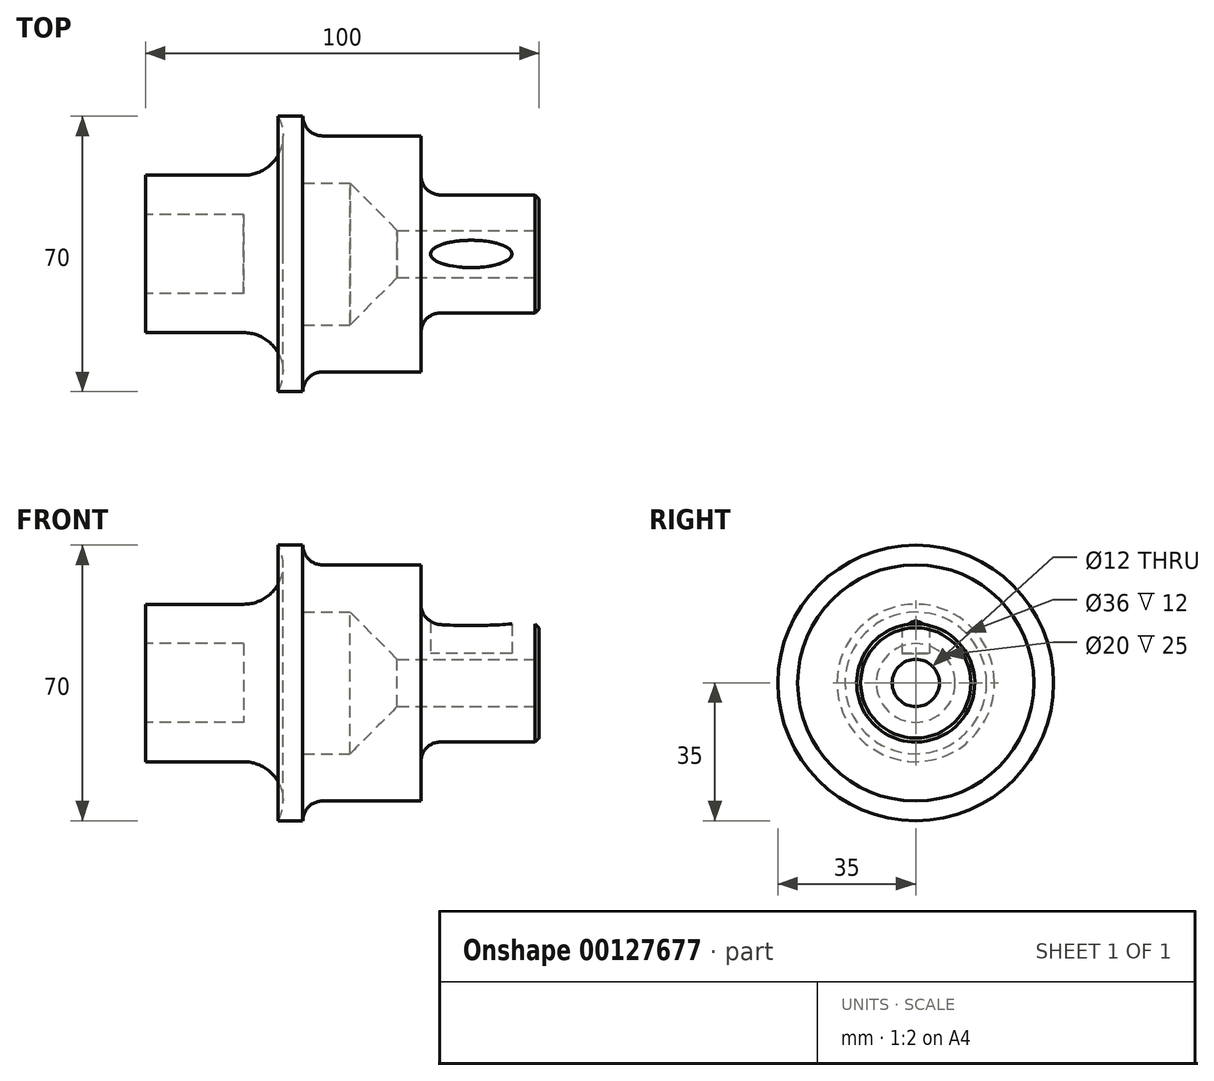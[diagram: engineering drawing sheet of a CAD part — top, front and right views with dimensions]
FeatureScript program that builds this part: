
annotation { "Feature Type Name" : "Feature", "Feature Type Description" : "" }
export const myFeature = defineFeature(function(context is Context, id is Id, definition is map)
    precondition{}
    {
        {
            var Q0;
            Q0=qCreatedBy(makeId("Front.planeOp"),FACE);
            var sketch = newSketch(context, id + "F0", { "sketchPlane" : qUnion([Q0])});
            skLineSegment(sketch, "E0", {"start": v(0, 0) * mm, "end": v(100, 0) * mm});
            skLineSegment(sketch, "E1", {"start": v(0, 0) * mm, "end": v(0, 20) * mm});
            skLineSegment(sketch, "E2", {"start": v(0, 20) * mm, "end": v(25, 20) * mm});
            skLineSegment(sketch, "E3", {"start": v(25, 20) * mm, "end": v(25, 35) * mm});
            skLineSegment(sketch, "E4", {"start": v(25, 35) * mm, "end": v(40, 35) * mm});
            skLineSegment(sketch, "E5", {"start": v(40, 35) * mm, "end": v(40, 30) * mm});
            skLineSegment(sketch, "E6", {"start": v(40, 30) * mm, "end": v(70, 30) * mm});
            skLineSegment(sketch, "E7", {"start": v(70, 30) * mm, "end": v(70, 15) * mm});
            skLineSegment(sketch, "E8", {"start": v(70, 15) * mm, "end": v(100, 15) * mm});
            skLineSegment(sketch, "E9", {"start": v(100, 15) * mm, "end": v(100, 0) * mm});
            skSolve(sketch);
        }
        {
            var Q0;
            Q0 = qSketchRegion(id + "F0", true);
            var Q1;
            Q1=sQuery(id+"F0.wireOp",EDGE,"E0");
            revolve(context, id + "F1", {"entities" : qUnion([Q0]), "axis" : qUnion([Q1]), "revolveType" : RevolveType.FULL});
        }
        {
            var Q0;
            Q0=makeQuery(id+"F1.opRevolve","SWEPT_FACE",FACE,{"disambiguationData":[OSD([sQuery(id+"F0.wireOp",EDGE,"E1")])]});
            var sketch = newSketch(context, id + "F2", { "sketchPlane" : qUnion([Q0])});
            skCircle(sketch, "E10", {"center": v(0, 0) * mm, "radius": 10 * mm});
            skSolve(sketch);
        }
        {
            var Q0;
            Q0 = qSketchRegion(id + "F2", true);
            extrude(context, id + "F3", {"entities" : qUnion([Q0]), "operationType" : NewBodyOperationType.REMOVE, "oppositeDirection" : true, "depth" : 25 * mm});
        }
        {
            var Q0;
            Q0=qCreatedBy(makeId("Front.planeOp"),FACE);
            var sketch = newSketch(context, id + "F4", { "sketchPlane" : qUnion([Q0])});
            skLineSegment(sketch, "E11", {"start": v(0, 0) * mm, "end": v(100, 0) * mm});
            skLineSegment(sketch, "E12", {"start": v(100, 0) * mm, "end": v(100, 6) * mm});
            skLineSegment(sketch, "E13", {"start": v(100, 6) * mm, "end": v(64, 6) * mm});
            skLineSegment(sketch, "E14", {"start": v(64, 6) * mm, "end": v(52, 18) * mm});
            skLineSegment(sketch, "E15", {"start": v(52, 18) * mm, "end": v(40, 18) * mm});
            skLineSegment(sketch, "E16", {"start": v(40, 18) * mm, "end": v(40, 0) * mm});
            skSolve(sketch);
        }
        {
            var Q0;
            Q0 = qSketchRegion(id + "F4", true);
            var Q1;
            Q1=sQuery(id+"F4.wireOp",EDGE,"E11");
            revolve(context, id + "F5", {"operationType" : NewBodyOperationType.REMOVE, "entities" : qUnion([Q0]), "axis" : qUnion([Q1]), "revolveType" : RevolveType.FULL, "oppositeDirection" : true});
        }
        {
            var Q0;
            Q0=qCreatedBy(makeId("Top.planeOp"),FACE);
            cPlane(context, id + "F6", {"entities" : qUnion([Q0]), "cplaneType" : CPlaneType.OFFSET, "offset" : 7.5 * mm, "width" : 150 * mm, "height" : 150 * mm});
        }
        {
            var Q0;
            Q0=qCreatedBy(id+"F6.planeOp",FACE);
            var sketch = newSketch(context, id + "F7", { "sketchPlane" : qUnion([Q0])});
            skEllipse(sketch, "E17", {"center": v(82.78, 0) * mm, "majorRadius": 10.35 * mm, "minorRadius": 3.48 * mm, "majorAxis": v(1, 0)});
            skSolve(sketch);
        }
        {
            var Q0;
            Q0 = qSketchRegion(id + "F7", true);
            extrude(context, id + "F8", {"entities" : qUnion([Q0]), "operationType" : NewBodyOperationType.REMOVE, "depth" : 25 * mm});
        }
        {
            var Q0;
            Q0=makeQuery(id+"F1.opRevolve","SWEPT_EDGE",EDGE,{"disambiguationData":[OSD([sQuery(id+"F0.wireOp",EDGE,"E5"),sQuery(id+"F0.wireOp",EDGE,"E6")])]});
            var Q1;
            Q1=makeQuery(id+"F1.opRevolve","SWEPT_EDGE",EDGE,{"disambiguationData":[OSD([sQuery(id+"F0.wireOp",EDGE,"E7"),sQuery(id+"F0.wireOp",EDGE,"E8")])]});
            fillet(context, id + "F9", {"entities" : qUnion([Q0, Q1]), "radius" : 5 * mm, "tangentPropagation" : true, "allowEdgeOverflow" : false});
        }
        {
            var Q0;
            Q0=makeQuery(id+"F1.opRevolve","SWEPT_EDGE",EDGE,{"disambiguationData":[OSD([sQuery(id+"F0.wireOp",EDGE,"E8"),sQuery(id+"F0.wireOp",EDGE,"E9")])]});
            var Q1;
            Q1=makeQuery(id+"F5.boolean.opBoolean","COPY",EDGE,{"derivedFrom":makeQuery(id+"F5.opRevolve","SWEPT_EDGE",EDGE,{"disambiguationData":[OSD([sQuery(id+"F4.wireOp",EDGE,"E12"),sQuery(id+"F4.wireOp",EDGE,"E13")])]})});
            chamfer(context, id + "F10", {"entities" : qUnion([Q0, Q1]), "chamferType" : ChamferType.OFFSET_ANGLE, "width" : 1 * mm, "oppositeDirection" : false, "angle" : 45 * degree, "tangentPropagation" : true});
        }
        {
            var Q0;
            Q0=qCreatedBy(makeId("Front.planeOp"),FACE);
            var sketch = newSketch(context, id + "F12", { "sketchPlane" : qUnion([Q0])});
            skCircle(sketch, "E18", {"center": v(25, 30) * mm, "radius": 10 * mm});
            skLineSegment(sketch, "E19", {"start": v(0, 0) * mm, "end": v(-16.6, 0) * mm});
            skSolve(sketch);
        }
        {
            var Q0;
            Q0 = qSketchRegion(id + "F12", true);
            var Q1;
            Q1=sQuery(id+"F12.wireOp",EDGE,"E19");
            revolve(context, id + "F11", {"operationType" : NewBodyOperationType.REMOVE, "entities" : qUnion([Q0]), "axis" : qUnion([Q1]), "revolveType" : RevolveType.FULL, "oppositeDirection" : true});
        }
    });
